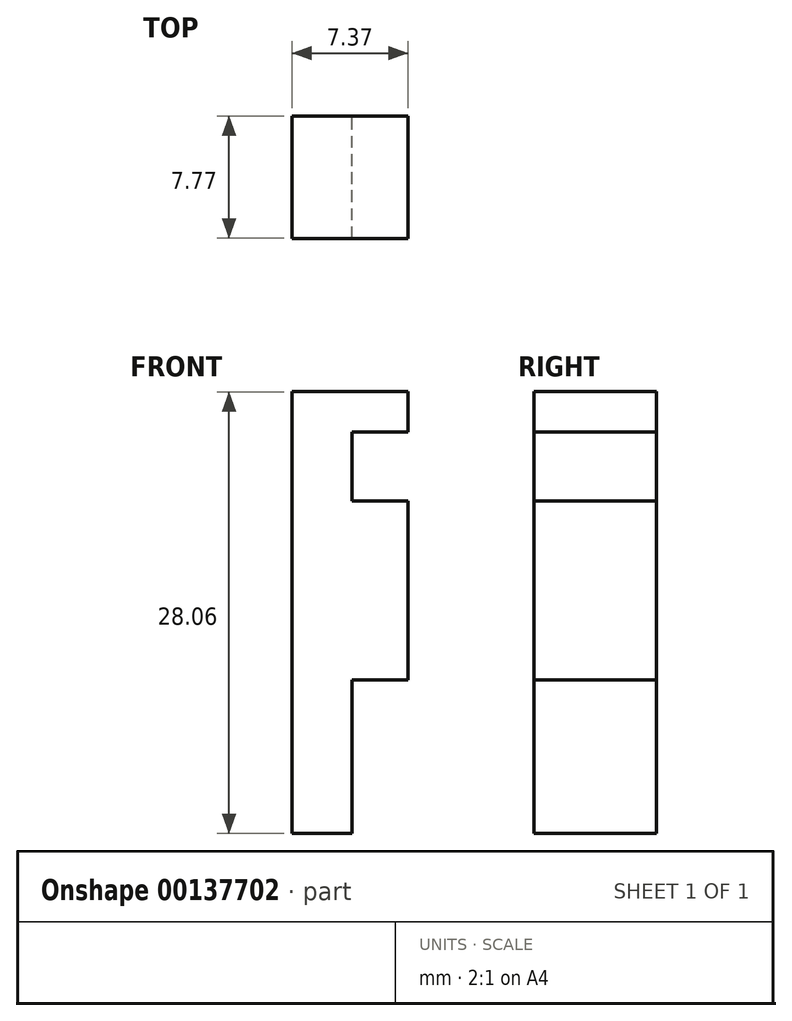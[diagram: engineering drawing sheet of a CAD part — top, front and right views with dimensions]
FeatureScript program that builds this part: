
annotation { "Feature Type Name" : "Feature", "Feature Type Description" : "" }
export const myFeature = defineFeature(function(context is Context, id is Id, definition is map)
    precondition{}
    {
        {
            var Q0;
            Q0=qCreatedBy(makeId("Front.planeOp"),FACE);
            var sketch = newSketch(context, id + "F0", { "sketchPlane" : qUnion([Q0])});
            skLineSegment(sketch, "E0", {"start": v(-27.06, -47.5) * mm, "end": v(-27.06, -43.12) * mm});
            skLineSegment(sketch, "E1", {"start": v(-27.06, -43.12) * mm, "end": v(-23.5, -43.12) * mm});
            skLineSegment(sketch, "E2", {"start": v(-23.5, -43.12) * mm, "end": v(-23.5, -40.56) * mm});
            skLineSegment(sketch, "E3", {"start": v(-30.87, -65.3) * mm, "end": v(-30.87, -68.62) * mm});
            skLineSegment(sketch, "E4", {"start": v(-27.06, -58.87) * mm, "end": v(-23.5, -58.87) * mm});
            skLineSegment(sketch, "E5", {"start": v(-27.06, -58.87) * mm, "end": v(-27.06, -68.62) * mm});
            skLineSegment(sketch, "E6", {"start": v(-27.06, -68.62) * mm, "end": v(-30.87, -68.62) * mm});
            skLineSegment(sketch, "E7", {"start": v(-23.5, -47.5) * mm, "end": v(-23.5, -58.87) * mm});
            skLineSegment(sketch, "E8", {"start": v(-23.5, -47.5) * mm, "end": v(-27.06, -47.5) * mm});
            skLineSegment(sketch, "E9", {"start": v(-30.87, -65.3) * mm, "end": v(-30.87, -40.56) * mm});
            skLineSegment(sketch, "E10", {"start": v(-30.87, -40.56) * mm, "end": v(-23.5, -40.56) * mm});
            skSolve(sketch);
        }
        {
            var Q0;
            Q0 = qSketchRegion(id + "F0", true);
            extrude(context, id + "F1", {"entities" : qUnion([Q0]), "depth" : 7.77 * mm});
        }
    });
